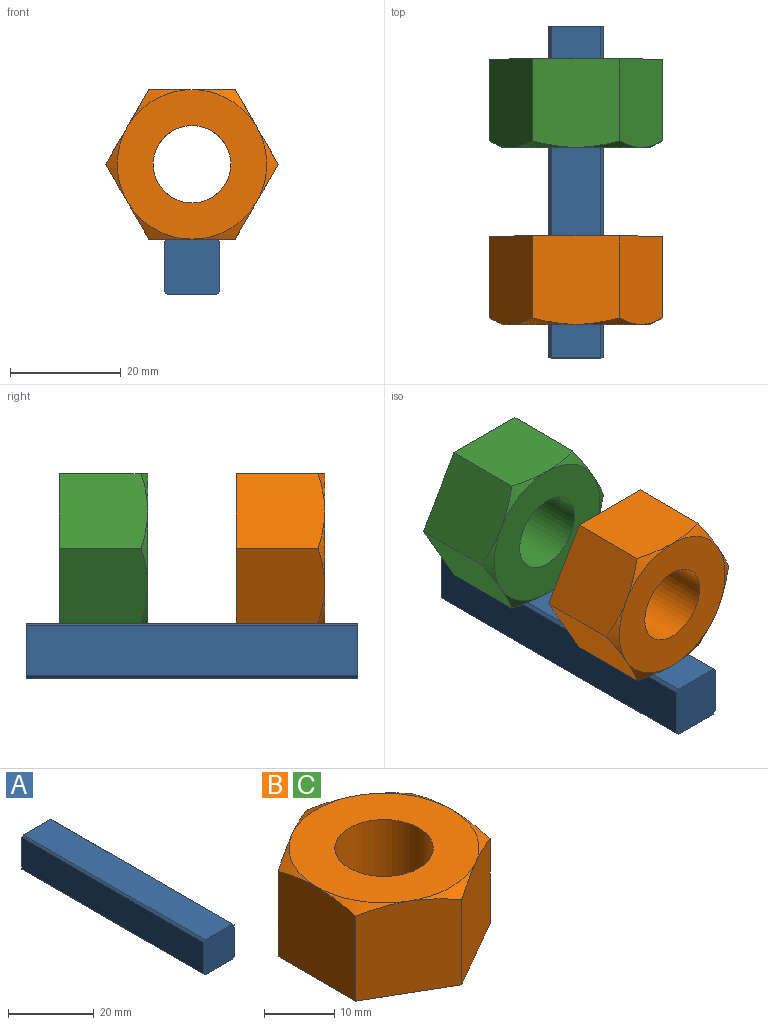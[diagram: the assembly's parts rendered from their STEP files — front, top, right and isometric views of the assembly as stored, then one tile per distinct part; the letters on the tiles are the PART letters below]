
ASSEMBLY  parts=3 mates=5
PART A: 10 faces, bbox 10x60x10 mm
  f0: plane 60x9mm, normal (0,0,-1), area 540mm2, adj f4,f5,f6,f8
  f1: plane 60x9mm, normal (1,0,0), area 540mm2, adj f4,f5,f8,f9
  f2: plane 60x9mm, normal (0,0,1), area 540mm2, adj f4,f5,f7,f9
  f3: plane 60x9mm, normal (-1,0,0), area 540mm2, adj f4,f5,f6,f7
  f4: plane 10x10mm, normal (0,-1,0), area 99.5mm2, adj f0,f1,f2,f3,f6,f7,f8,f9
  f5: plane 10x10mm, normal (0,1,0), area 99.5mm2, adj f0,f1,f2,f3,f6,f7,f8,f9
  f6: plane 60x0.5mm, normal (-0.71,0,-0.71), area 42.4mm2, adj f0,f3,f4,f5
  f7: plane 60x0.5mm, normal (-0.71,0,0.71), area 42.4mm2, adj f2,f3,f4,f5
  f8: plane 60x0.5mm, normal (0.71,0,-0.71), area 42.4mm2, adj f0,f1,f4,f5
  f9: plane 60x0.5mm, normal (0.71,0,0.71), area 42.4mm2, adj f1,f2,f4,f5
PART B: 15 faces, bbox 31.2x31.2x16 mm
  f0: plane 16x13.51mm, normal (0.5,0.87,0), area 243.1mm2, adj f1,f5,f6,f7,f12
  f1: plane 16x13.51mm, normal (-0.5,0.87,0), area 243.1mm2, adj f0,f2,f6,f11,f12
  f2: plane 16x15.61mm, normal (-1,0,0), area 243.1mm2, adj f1,f3,f6,f10,f11
  f3: plane 16x13.51mm, normal (-0.5,-0.87,0), area 243.1mm2, adj f2,f4,f6,f9,f10
  f4: plane 16x13.51mm, normal (0.5,-0.87,0), area 243.1mm2, adj f3,f5,f6,f8,f9
  f5: plane 16x15.61mm, normal (1,0,0), area 243.1mm2, adj f0,f4,f6,f7,f8
  f6: plane 31.2x27.02mm, normal (0,0,-1), area 478.3mm2, adj f0,f1,f2,f3,f4,f5,f14
  f7: cone r=16mm half-angle=60deg, axis (0,0,-1), area 11.3mm2, adj f0,f5,f13
  f8: cone r=16mm half-angle=60deg, axis (0,0,-1), area 11.3mm2, adj f4,f5,f13
  f9: cone r=16mm half-angle=60deg, axis (0,0,-1), area 11.3mm2, adj f3,f4,f13
  f10: cone r=16mm half-angle=60deg, axis (0,0,-1), area 11.3mm2, adj f2,f3,f13
  f11: cone r=16mm half-angle=60deg, axis (0,0,-1), area 11.3mm2, adj f1,f2,f13
  f12: cone r=16mm half-angle=60deg, axis (0,0,-1), area 11.3mm2, adj f0,f1,f13
  f13: plane 27.02x27.02mm, normal (0,0,1), area 419.5mm2, adj f7,f8,f9,f10,f11,f12,f14
  f14: cylinder r=7mm len=16mm, axis (0,0,1), area 703.7mm2, adj f6,f13
PART C: same geometry as B
PLACE A t=(0,24,-18.51)mm
PLACE B rot(axis=(0.94,0.25,-0.25),93.8deg) t=(0,0,0)mm
PLACE C rot(axis=(0.58,0.58,-0.58),120deg) t=(0,32,0)mm
MATE planar A.f4 <-> B.f7  axis (0,-1,0) through (0,-6,-18.51)mm
MATE planar C.f2 <-> B.f1  axis (0,0,1) through (0,40.2,13.51)mm
MATE cylindrical C.f7 <-> B.f7  axis (0,-1,0) through (0,32,0)mm
MATE planar C.f7 <-> B.f7  axis (0,-1,0) through (0,32,0)mm
MATE planar A.f2 <-> B.f4  axis (0,0,1) through (0,24,-13.51)mm
